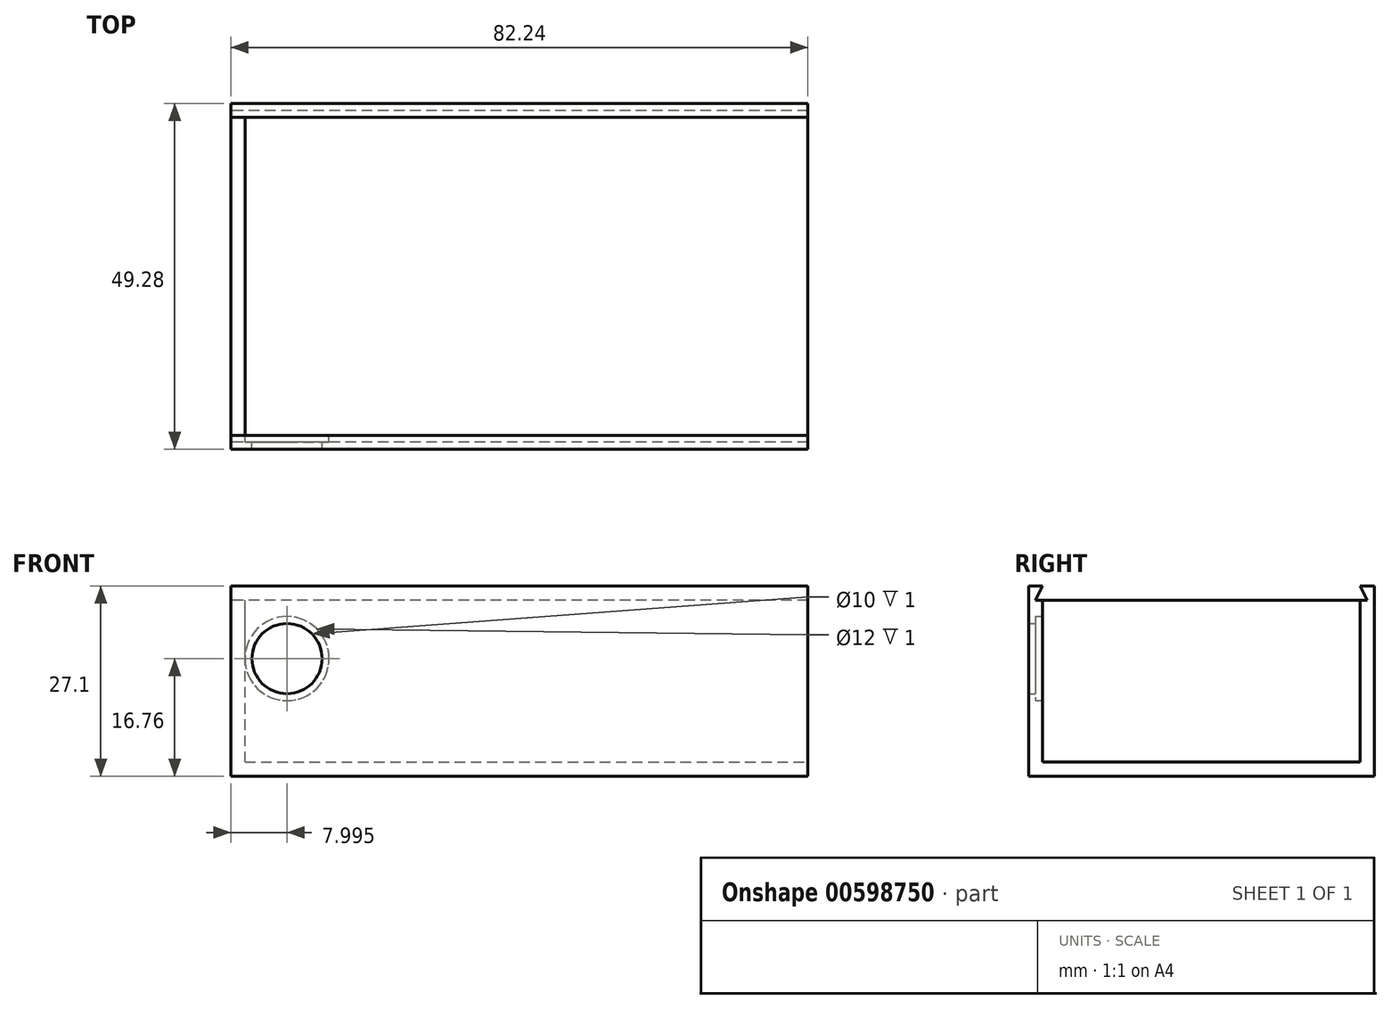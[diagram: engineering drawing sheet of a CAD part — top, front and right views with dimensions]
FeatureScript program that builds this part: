
annotation { "Feature Type Name" : "Feature", "Feature Type Description" : "" }
export const myFeature = defineFeature(function(context is Context, id is Id, definition is map)
    precondition{}
    {
        {
            var Q0;
            Q0=qCreatedBy(makeId("Top.planeOp"),FACE);
            var sketch = newSketch(context, id + "F0", { "sketchPlane" : qUnion([Q0])});
            skLineSegment(sketch, "E0.bottom", {"start": v(-42.12, 24.64) * mm, "end": v(42.13, 24.64) * mm});
            skLineSegment(sketch, "E0.top", {"start": v(-42.13, -24.64) * mm, "end": v(42.12, -24.64) * mm});
            skLineSegment(sketch, "E0.left", {"start": v(-42.12, 24.64) * mm, "end": v(-42.13, -24.64) * mm});
            skLineSegment(sketch, "E0.right", {"start": v(42.13, 24.64) * mm, "end": v(42.12, -24.64) * mm});
            skPoint(sketch, "E0.middle", {"position": v(0, 0) * mm});
            skSolve(sketch);
        }
        {
            var Q0;
            Q0=makeQuery(id+"F0.imprint","IMPRINT",FACE,{"disambiguationData":[TD([[makeQuery(id+"F0.imprint","IMPRINT",EDGE,{"derivedFrom":sQuery(id+"F0.wireOp",EDGE,"E0.bottom")}),-1.0]])]});
            extrude(context, id + "F1", {"entities" : qUnion([Q0]), "depth" : 27.1 * mm, "offsetDistance" : 25 * mm});
        }
        {
            var Q0;
            Q0=makeQuery(id+"F1.opExtrude","CAP_FACE",FACE,{"disambiguationData":[OSD([sQuery(id+"F0.wireOp",EDGE,"E0.bottom"),sQuery(id+"F0.wireOp",EDGE,"E0.top"),sQuery(id+"F0.wireOp",EDGE,"E0.left"),sQuery(id+"F0.wireOp",EDGE,"E0.right")])],"isStart":false});
            var sketch = newSketch(context, id + "F2", { "sketchPlane" : qUnion([Q0])});
            skLineSegment(sketch, "E1.bottom", {"start": v(-40.12, 22.64) * mm, "end": v(40.13, 22.64) * mm});
            skLineSegment(sketch, "E1.top", {"start": v(-40.13, -22.64) * mm, "end": v(40.12, -22.64) * mm});
            skLineSegment(sketch, "E1.left", {"start": v(-40.12, 22.64) * mm, "end": v(-40.13, -22.64) * mm});
            skLineSegment(sketch, "E1.right", {"start": v(40.13, 22.64) * mm, "end": v(40.12, -22.64) * mm});
            skPoint(sketch, "E1.middle", {"position": v(0, 0) * mm});
            skSolve(sketch);
        }
        {
            var Q0;
            Q0=makeQuery(id+"F2.imprint","IMPRINT",FACE,{"disambiguationData":[TD([[makeQuery(id+"F2.imprint","IMPRINT",EDGE,{"derivedFrom":sQuery(id+"F2.wireOp",EDGE,"E1.bottom")}),-1.0]])]});
            extrude(context, id + "F3", {"entities" : qUnion([Q0]), "operationType" : NewBodyOperationType.REMOVE, "oppositeDirection" : true, "depth" : 25.1 * mm, "offsetDistance" : 25 * mm});
        }
        {
            var Q0;
            Q0=makeQuery(id+"F3.boolean.opBoolean","COPY",FACE,{"derivedFrom":makeQuery(id+"F3.opExtrude","SWEPT_FACE",FACE,{"disambiguationData":[OSD([sQuery(id+"F2.wireOp",EDGE,"E1.right")])]})});
            var sketch = newSketch(context, id + "F4", { "sketchPlane" : qUnion([Q0])});
            skLineSegment(sketch, "E2", {"start": v(-22.64, 14.55) * mm, "end": v(-13.55, 14.55) * mm});
            skLineSegment(sketch, "E3.bottom", {"start": v(-22.64, 20.2) * mm, "end": v(-4.46, 20.2) * mm});
            skLineSegment(sketch, "E3.top", {"start": v(-22.64, 8.9) * mm, "end": v(-4.46, 8.9) * mm});
            skLineSegment(sketch, "E3.left", {"start": v(-22.64, 20.2) * mm, "end": v(-22.64, 8.9) * mm});
            skLineSegment(sketch, "E3.right", {"start": v(-4.46, 20.2) * mm, "end": v(-4.46, 8.9) * mm});
            skPoint(sketch, "E3.middle", {"position": v(-13.55, 14.55) * mm});
            skSolve(sketch);
        }
        {
            var Q0;
            {var subQ2=sQuery(id+"F4.wireOp",EDGE,"E3.bottom");Q0=makeQuery(id+"F4.imprint","IMPRINT",FACE,{"disambiguationData":[TD([[makeQuery(id+"F4.imprint","IMPRINT",EDGE,{"derivedFrom":subQ2}),-1.0]])]});}
            extrude(context, id + "F5", {"entities" : qUnion([Q0]), "operationType" : NewBodyOperationType.REMOVE, "oppositeDirection" : true, "depth" : 25 * mm, "offsetDistance" : 25 * mm, "hasSecondDirection" : true, "secondDirectionOppositeDirection" : false, "secondDirectionDepth" : 25 * mm});
        }
        {
            var Q0;
            Q0=makeQuery(id+"F3.boolean.opBoolean","COPY",FACE,{"derivedFrom":makeQuery(id+"F3.opExtrude","CAP_FACE",FACE,{"disambiguationData":[OSD([sQuery(id+"F2.wireOp",EDGE,"E1.bottom"),sQuery(id+"F2.wireOp",EDGE,"E1.top"),sQuery(id+"F2.wireOp",EDGE,"E1.left"),sQuery(id+"F2.wireOp",EDGE,"E1.right")])],"isStart":false})});
            var sketch = newSketch(context, id + "F6", { "sketchPlane" : qUnion([Q0])});
            skLineSegment(sketch, "E4", {"start": v(-40.13, -22.64) * mm, "end": v(-40.12, 7.36) * mm});
            skLineSegment(sketch, "E5", {"start": v(-40.13, -22.64) * mm, "end": v(-25.12, -22.64) * mm});
            skSolve(sketch);
        }
        {
            var Q0;
            Q0=makeQuery(id+"F3.boolean.opBoolean","COPY",FACE,{"derivedFrom":makeQuery(id+"F3.opExtrude","SWEPT_FACE",FACE,{"disambiguationData":[OSD([sQuery(id+"F2.wireOp",EDGE,"E1.top")])]})});
            var sketch = newSketch(context, id + "F7", { "sketchPlane" : qUnion([Q0])});
            skLineSegment(sketch, "E6", {"start": v(40.13, 2) * mm, "end": v(34.13, 2) * mm});
            skLineSegment(sketch, "E7", {"start": v(34.13, 2) * mm, "end": v(34.13, 16.76) * mm});
            skSolve(sketch);
        }
        {
            var Q0;
            Q0=sQuery(id+"F7.wireOp",VERTEX,"E7.end");
            var Q1;
            Q1=makeQuery(id+"F1.opExtrude","SWEPT_BODY",BODY,{"disambiguationData":[OSD([sQuery(id+"F0.wireOp",EDGE,"E0.bottom"),sQuery(id+"F0.wireOp",EDGE,"E0.top"),sQuery(id+"F0.wireOp",EDGE,"E0.left"),sQuery(id+"F0.wireOp",EDGE,"E0.right")])]});
            hole(context, id + "F8", {"style" : HoleStyle.C_BORE, "endStyle" : HoleEndStyle.BLIND, "holeDiameter" : 10 * mm, "cBoreDiameter" : 12 * mm, "cBoreDepth" : 1 * mm, "majorDiameter" : 5 * mm, "holeDepth" : 2 * mm, "isTappedThrough" : true, "tappedDepth" : 12 * mm, "tapClearance" : 3, "locations" : qUnion([Q0]), "scope" : qUnion([Q1])});
        }
        {
            var Q0;
            Q0=makeQuery(id+"F1.opExtrude","CAP_FACE",FACE,{"disambiguationData":[OSD([sQuery(id+"F0.wireOp",EDGE,"E0.bottom"),sQuery(id+"F0.wireOp",EDGE,"E0.top"),sQuery(id+"F0.wireOp",EDGE,"E0.left"),sQuery(id+"F0.wireOp",EDGE,"E0.right")])],"isStart":false});
            var sketch = newSketch(context, id + "F9", { "sketchPlane" : qUnion([Q0])});
            skLineSegment(sketch, "E8.bottom", {"start": v(-42.12, 22.64) * mm, "end": v(-38.12, 22.64) * mm});
            skLineSegment(sketch, "E8.top", {"start": v(-42.12, -22.64) * mm, "end": v(-38.12, -22.64) * mm});
            skLineSegment(sketch, "E8.left", {"start": v(-42.12, 22.64) * mm, "end": v(-42.12, -22.64) * mm});
            skLineSegment(sketch, "E8.right", {"start": v(-38.12, 22.64) * mm, "end": v(-38.12, -22.64) * mm});
            skPoint(sketch, "E8.middle", {"position": v(-40.12, 0) * mm});
            skSolve(sketch);
        }
        {
            var Q0;
            {var subQ2=sQuery(id+"F9.wireOp",EDGE,"E8.left");Q0=makeQuery(id+"F9.imprint","IMPRINT",FACE,{"disambiguationData":[TD([[makeQuery(id+"F9.imprint","IMPRINT",EDGE,{"derivedFrom":subQ2}),1.0]])]});}
            extrude(context, id + "F10", {"entities" : qUnion([Q0]), "operationType" : NewBodyOperationType.REMOVE, "oppositeDirection" : true, "depth" : 2 * mm, "offsetDistance" : 25 * mm});
        }
        {
            var Q0;
            Q0=makeQuery(id+"F1.opExtrude","SWEPT_FACE",FACE,{"disambiguationData":[OSD([sQuery(id+"F0.wireOp",EDGE,"E0.left")])]});
            var sketch = newSketch(context, id + "F11", { "sketchPlane" : qUnion([Q0])});
            skLineSegment(sketch, "E9", {"start": v(-23.64, 25.1) * mm, "end": v(-22.64, 27.1) * mm});
            skPoint(sketch, "E9.startSnap0", {"position": v(-23.64, 27.1) * mm});
            skLineSegment(sketch, "E10", {"start": v(-23.64, 25.1) * mm, "end": v(-22.64, 25.1) * mm});
            skLineSegment(sketch, "E11", {"start": v(23.64, 25.1) * mm, "end": v(22.64, 27.1) * mm});
            skPoint(sketch, "E11.startSnap0", {"position": v(23.64, 27.1) * mm});
            skLineSegment(sketch, "E12", {"start": v(23.64, 25.1) * mm, "end": v(22.64, 25.1) * mm});
            skSolve(sketch);
        }
        {
            var Q0;
            Q0=makeQuery(id+"F11.imprint","IMPRINT",FACE,{"disambiguationData":[TD([[makeQuery(id+"F11.imprint","IMPRINT",EDGE,{"derivedFrom":sQuery(id+"F11.wireOp",EDGE,"E11")}),1.0]])]});
            var Q1;
            Q1=makeQuery(id+"F11.imprint","IMPRINT",FACE,{"disambiguationData":[TD([[makeQuery(id+"F11.imprint","IMPRINT",EDGE,{"derivedFrom":sQuery(id+"F11.wireOp",EDGE,"E9")}),-1.0]])]});
            extrude(context, id + "F12", {"entities" : qUnion([Q0, Q1]), "operationType" : NewBodyOperationType.REMOVE, "oppositeDirection" : true, "depth" : 82.25 * mm, "offsetDistance" : 25 * mm});
        }
        {
            var Q0;
            Q0=makeQuery(id+"F1.opExtrude","SWEPT_FACE",FACE,{"disambiguationData":[OSD([sQuery(id+"F0.wireOp",EDGE,"E0.right")])]});
            var sketch = newSketch(context, id + "F13", { "sketchPlane" : qUnion([Q0])});
            skLineSegment(sketch, "E13.bottom", {"start": v(-24.64, 27.1) * mm, "end": v(24.64, 27.1) * mm});
            skLineSegment(sketch, "E13.top", {"start": v(-24.64, 0) * mm, "end": v(24.64, 0) * mm});
            skLineSegment(sketch, "E13.left", {"start": v(-24.64, 27.1) * mm, "end": v(-24.64, 0) * mm});
            skLineSegment(sketch, "E13.right", {"start": v(24.64, 27.1) * mm, "end": v(24.64, 0) * mm});
            skSolve(sketch);
        }
        {
            var Q0;
            Q0=makeQuery(id+"F13.imprint","IMPRINT",FACE,{"disambiguationData":[TD([[makeQuery(id+"F13.imprint","IMPRINT",EDGE,{"derivedFrom":sQuery(id+"F13.wireOp",EDGE,"E13.bottom")}),1.0]])]});
            extrude(context, id + "F14", {"entities" : qUnion([Q0]), "operationType" : NewBodyOperationType.REMOVE, "oppositeDirection" : true, "depth" : 2 * mm, "offsetDistance" : 25 * mm});
        }
    });
